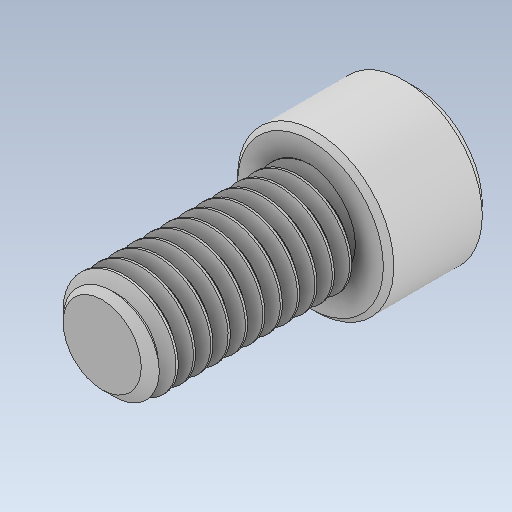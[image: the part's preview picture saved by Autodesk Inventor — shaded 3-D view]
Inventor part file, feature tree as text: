
AUTODESK INVENTOR PART (.ipt)
format: ipt  version: 2021 (Build 250183000, 183)  size: 566,784 bytes
history: native  units: in
note: dims shown in document units (in); Inventor stores cm internally (conversion verified against a paired STEP export)
features: chamfer x1
ambient origin geometry x8: Origin, YZ Plane, XZ Plane, XY Plane, X Axis, Y Axis, Z Axis, Center Point
bodies: Solid1 (feature_tree)
feature tree (1):
  chamfer  "Chamfer2"  [1 undecoded]
note: 1 required parameter value undecoded (feature->parameter linkage not recoverable at this tier; creation-order binding heuristic only, values carry confidence <= 0.55)
